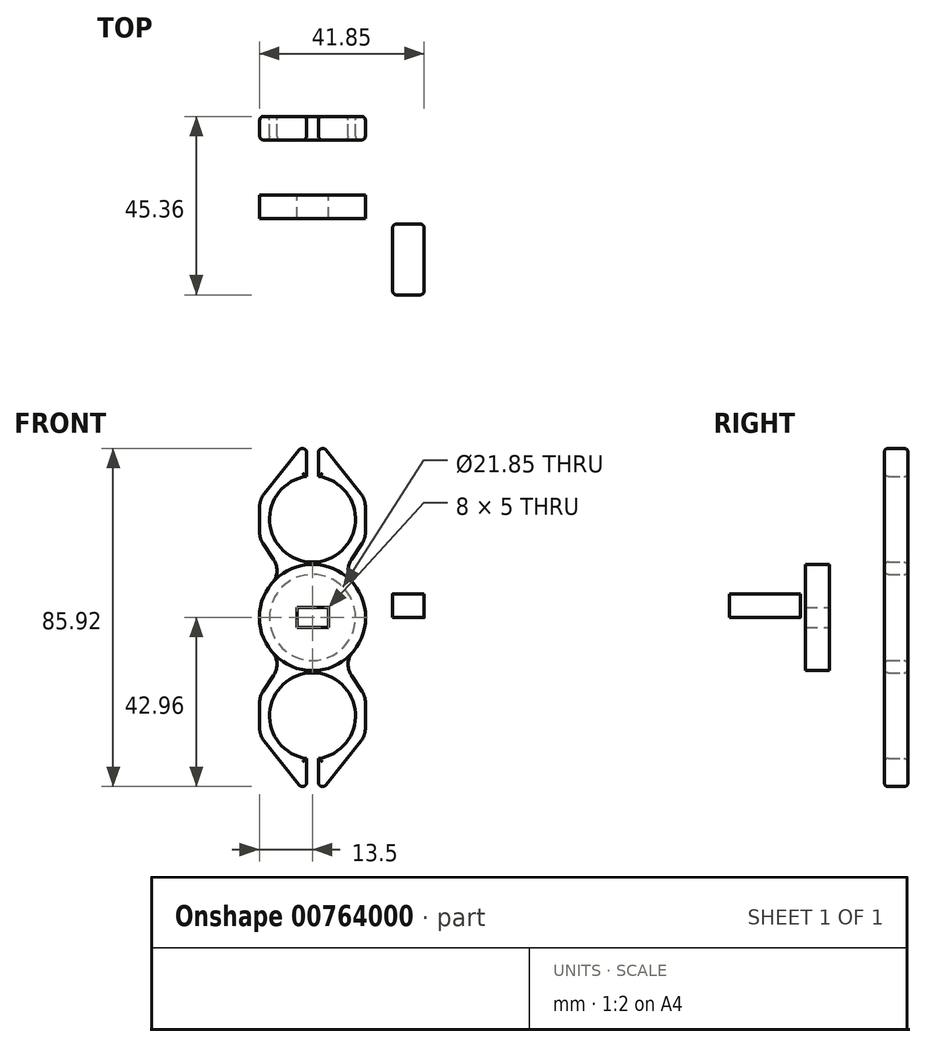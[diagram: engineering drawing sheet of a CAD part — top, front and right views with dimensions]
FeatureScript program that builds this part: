
annotation { "Feature Type Name" : "Feature", "Feature Type Description" : "" }
export const myFeature = defineFeature(function(context is Context, id is Id, definition is map)
    precondition{}
    {
        {
            var Q0;
            Q0=qCreatedBy(makeId("Front.planeOp"),FACE);
            var sketch = newSketch(context, id + "F0", { "sketchPlane" : qUnion([Q0])});
            skCircle(sketch, "E0", {"center": v(0, 0) * mm, "radius": 10.93 * mm});
            skLineSegment(sketch, "E1", {"start": v(0, 0) * mm, "end": v(0, 25) * mm, "construction": true});
            skArc(sketch, "E2", {"start": v(-1.5, 35.32) * mm, "mid": v(0, 14.58) * mm, "end": v(1.5, 35.32) * mm});
            skArc(sketch, "E3.1.0", {"start": v(1.5, -35.32) * mm, "mid": v(0, -14.58) * mm, "end": v(-1.5, -35.32) * mm});
            skLineSegment(sketch, "E4.left", {"start": v(1.5, -41.86) * mm, "end": v(1.5, -35.32) * mm});
            skLineSegment(sketch, "E4.right", {"start": v(-1.5, -41.86) * mm, "end": v(-1.5, -35.32) * mm});
            skLineSegment(sketch, "E5.left", {"start": v(13.42, -28.26) * mm, "end": v(13.42, -21.51) * mm});
            skLineSegment(sketch, "E5.right", {"start": v(-13.42, -28.26) * mm, "end": v(-13.42, -21.51) * mm});
            skLineSegment(sketch, "E6.left", {"start": v(13.42, 21.51) * mm, "end": v(13.42, 28.26) * mm});
            skLineSegment(sketch, "E6.right", {"start": v(-13.42, 21.51) * mm, "end": v(-13.42, 28.26) * mm});
            skLineSegment(sketch, "E7", {"start": v(12.33, 31.37) * mm, "end": v(3.45, 42.54) * mm});
            skLineSegment(sketch, "E8", {"start": v(-3.45, 42.54) * mm, "end": v(-12.33, 31.37) * mm});
            skArc(sketch, "E9", {"start": v(10.23, -8.68) * mm, "mid": v(13.42, 0) * mm, "end": v(10.23, 8.68) * mm});
            skLineSegment(sketch, "E10", {"start": v(12.33, -31.37) * mm, "end": v(3.45, -42.54) * mm});
            skLineSegment(sketch, "E11", {"start": v(-3.45, -42.54) * mm, "end": v(-12.33, -31.37) * mm});
            skLineSegment(sketch, "E12", {"start": v(12.58, -18.74) * mm, "end": v(9.88, -14.7) * mm});
            skLineSegment(sketch, "E13", {"start": v(-9.88, -14.7) * mm, "end": v(-12.58, -18.74) * mm});
            skLineSegment(sketch, "E14", {"start": v(12.58, 18.74) * mm, "end": v(9.88, 14.7) * mm});
            skLineSegment(sketch, "E15", {"start": v(-9.88, 14.7) * mm, "end": v(-12.58, 18.74) * mm});
            skLineSegment(sketch, "E16.trimOffspring", {"start": v(1.5, 35.32) * mm, "end": v(1.5, 41.86) * mm});
            skLineSegment(sketch, "E17.trimOffspring", {"start": v(-1.5, 35.32) * mm, "end": v(-1.5, 41.86) * mm});
            skArc(sketch, "E18.trimOffspring", {"start": v(-10.23, 8.68) * mm, "mid": v(-13.42, 0) * mm, "end": v(-10.23, -8.68) * mm});
            skPoint(sketch, "E19.visualSharp", {"position": v(13.42, 30) * mm});
            skArc(sketch, "E19.filletArc", {"start": v(13.42, 28.26) * mm, "mid": v(13.14, 29.9) * mm, "end": v(12.33, 31.37) * mm});
            skPoint(sketch, "E20.visualSharp", {"position": v(13.42, 20) * mm});
            skArc(sketch, "E20.filletArc", {"start": v(12.58, 18.74) * mm, "mid": v(13.2, 20.07) * mm, "end": v(13.42, 21.51) * mm});
            skPoint(sketch, "E21.visualSharp", {"position": v(-13.42, 20) * mm});
            skArc(sketch, "E21.filletArc", {"start": v(-13.42, 21.51) * mm, "mid": v(-13.2, 20.07) * mm, "end": v(-12.58, 18.74) * mm});
            skPoint(sketch, "E22.visualSharp", {"position": v(-13.42, 30) * mm});
            skArc(sketch, "E22.filletArc", {"start": v(-12.33, 31.37) * mm, "mid": v(-13.14, 29.9) * mm, "end": v(-13.42, 28.26) * mm});
            skPoint(sketch, "E23.visualSharp", {"position": v(-1.5, 45) * mm});
            skArc(sketch, "E23.filletArc", {"start": v(-1.5, 41.86) * mm, "mid": v(-2.23, 42.9) * mm, "end": v(-3.45, 42.54) * mm});
            skPoint(sketch, "E24.visualSharp", {"position": v(1.5, 45) * mm});
            skArc(sketch, "E24.filletArc", {"start": v(3.45, 42.54) * mm, "mid": v(2.23, 42.9) * mm, "end": v(1.5, 41.86) * mm});
            skPoint(sketch, "E25.visualSharp", {"position": v(13.42, -20) * mm});
            skArc(sketch, "E25.filletArc", {"start": v(13.42, -21.51) * mm, "mid": v(13.2, -20.07) * mm, "end": v(12.58, -18.74) * mm});
            skPoint(sketch, "E26.visualSharp", {"position": v(13.42, -30) * mm});
            skArc(sketch, "E26.filletArc", {"start": v(12.33, -31.37) * mm, "mid": v(13.14, -29.9) * mm, "end": v(13.42, -28.26) * mm});
            skPoint(sketch, "E27.visualSharp", {"position": v(1.5, -45) * mm});
            skArc(sketch, "E27.filletArc", {"start": v(1.5, -41.86) * mm, "mid": v(2.23, -42.9) * mm, "end": v(3.45, -42.54) * mm});
            skPoint(sketch, "E28.visualSharp", {"position": v(-1.5, -45) * mm});
            skArc(sketch, "E28.filletArc", {"start": v(-3.45, -42.54) * mm, "mid": v(-2.23, -42.9) * mm, "end": v(-1.5, -41.86) * mm});
            skPoint(sketch, "E29.visualSharp", {"position": v(-13.42, -30) * mm});
            skArc(sketch, "E29.filletArc", {"start": v(-13.42, -28.26) * mm, "mid": v(-13.14, -29.9) * mm, "end": v(-12.33, -31.37) * mm});
            skPoint(sketch, "E30.visualSharp", {"position": v(-13.42, -20) * mm});
            skArc(sketch, "E30.filletArc", {"start": v(-12.58, -18.74) * mm, "mid": v(-13.2, -20.07) * mm, "end": v(-13.42, -21.51) * mm});
            skPoint(sketch, "E31.visualSharp", {"position": v(7.5, -11.13) * mm});
            skArc(sketch, "E31.filletArc", {"start": v(10.23, -8.68) * mm, "mid": v(9.05, -11.63) * mm, "end": v(9.88, -14.7) * mm});
            skPoint(sketch, "E32.visualSharp", {"position": v(-7.5, -11.13) * mm});
            skArc(sketch, "E32.filletArc", {"start": v(-9.88, -14.7) * mm, "mid": v(-9.05, -11.63) * mm, "end": v(-10.23, -8.68) * mm});
            skPoint(sketch, "E33.visualSharp", {"position": v(7.5, 11.13) * mm});
            skArc(sketch, "E33.filletArc", {"start": v(9.88, 14.7) * mm, "mid": v(9.05, 11.63) * mm, "end": v(10.23, 8.68) * mm});
            skPoint(sketch, "E34.visualSharp", {"position": v(-7.5, 11.13) * mm});
            skArc(sketch, "E34.filletArc", {"start": v(-10.23, 8.68) * mm, "mid": v(-9.05, 11.63) * mm, "end": v(-9.88, 14.7) * mm});
            skCircle(sketch, "E35", {"center": v(0, 25) * mm, "radius": 10.93 * mm});
            skCircle(sketch, "E36", {"center": v(0, -25) * mm, "radius": 10.93 * mm});
            skSolve(sketch);
        }
        {
            var Q0;
            Q0=makeQuery(id+"F0.imprint","IMPRINT",FACE,{"disambiguationData":[TD([[makeQuery(id+"F0.imprint","IMPRINT",EDGE,{"derivedFrom":sQuery(id+"F0.wireOp",EDGE,"E0")}),-1.0]])]});
            extrude(context, id + "F1", {"entities" : qUnion([Q0]), "depth" : 6 * mm, "offsetDistance" : 25 * mm});
        }
        {
            var Q0;
            Q0=makeQuery(id+"F1.opExtrude","CAP_FACE",FACE,{"disambiguationData":[OSD([sQuery(id+"F0.wireOp",EDGE,"E0"),sQuery(id+"F0.wireOp",EDGE,"E2"),sQuery(id+"F0.wireOp",EDGE,"E3.1.0"),sQuery(id+"F0.wireOp",EDGE,"E3.2.0"),sQuery(id+"F0.wireOp",EDGE,"E3.3.0"),sQuery(id+"F0.wireOp",EDGE,"E3.4.0"),sQuery(id+"F0.wireOp",EDGE,"6w4LuyIg-Judz-7qcx-iNhM-kCVs0XRHMAQz.left"),sQuery(id+"F0.wireOp",EDGE,"6w4LuyIg-Judz-7qcx-iNhM-kCVs0XRHMAQz.right"),sQuery(id+"F0.wireOp",EDGE,"GuxD1Two-tXSI-jhGi-diOq-QsG6SmieNdRW"),sQuery(id+"F0.wireOp",EDGE,"9e989a9f-be13-4d0f-822f-95c7c0624428.1.0"),sQuery(id+"F0.wireOp",EDGE,"9e989a9f-be13-4d0f-822f-95c7c0624428.1.1"),sQuery(id+"F0.wireOp",EDGE,"9e989a9f-be13-4d0f-822f-95c7c0624428.1.2"),sQuery(id+"F0.wireOp",EDGE,"9e989a9f-be13-4d0f-822f-95c7c0624428.2.0"),sQuery(id+"F0.wireOp",EDGE,"9e989a9f-be13-4d0f-822f-95c7c0624428.2.1"),sQuery(id+"F0.wireOp",EDGE,"9e989a9f-be13-4d0f-822f-95c7c0624428.2.2"),sQuery(id+"F0.wireOp",EDGE,"9e989a9f-be13-4d0f-822f-95c7c0624428.3.0"),sQuery(id+"F0.wireOp",EDGE,"9e989a9f-be13-4d0f-822f-95c7c0624428.3.1"),sQuery(id+"F0.wireOp",EDGE,"9e989a9f-be13-4d0f-822f-95c7c0624428.3.2"),sQuery(id+"F0.wireOp",EDGE,"9e989a9f-be13-4d0f-822f-95c7c0624428.4.0"),sQuery(id+"F0.wireOp",EDGE,"9e989a9f-be13-4d0f-822f-95c7c0624428.4.1"),sQuery(id+"F0.wireOp",EDGE,"9e989a9f-be13-4d0f-822f-95c7c0624428.4.2"),sQuery(id+"F0.wireOp",EDGE,"486a15bc-75c9-41d0-808c-e5c4775e6e80.filletArc"),sQuery(id+"F0.wireOp",EDGE,"d314a861-2769-46d2-9bec-117903992242.filletArc"),sQuery(id+"F0.wireOp",EDGE,"5d220be9-c9be-4508-b7a3-f434c5fdea58.filletArc"),sQuery(id+"F0.wireOp",EDGE,"2974d6c2-e4a2-45df-9bc2-224e587c2884.filletArc"),sQuery(id+"F0.wireOp",EDGE,"3265ed39-f9f2-4246-9e43-8a9d8c4dec78.filletArc")])],"isStart":false});
            var Q1;
            Q1=makeQuery(id+"F1.opExtrude","CAP_FACE",FACE,{"disambiguationData":[OSD([sQuery(id+"F0.wireOp",EDGE,"E0"),sQuery(id+"F0.wireOp",EDGE,"E2"),sQuery(id+"F0.wireOp",EDGE,"E3.1.0"),sQuery(id+"F0.wireOp",EDGE,"E3.2.0"),sQuery(id+"F0.wireOp",EDGE,"E3.3.0"),sQuery(id+"F0.wireOp",EDGE,"E3.4.0"),sQuery(id+"F0.wireOp",EDGE,"6w4LuyIg-Judz-7qcx-iNhM-kCVs0XRHMAQz.left"),sQuery(id+"F0.wireOp",EDGE,"6w4LuyIg-Judz-7qcx-iNhM-kCVs0XRHMAQz.right"),sQuery(id+"F0.wireOp",EDGE,"GuxD1Two-tXSI-jhGi-diOq-QsG6SmieNdRW"),sQuery(id+"F0.wireOp",EDGE,"9e989a9f-be13-4d0f-822f-95c7c0624428.1.0"),sQuery(id+"F0.wireOp",EDGE,"9e989a9f-be13-4d0f-822f-95c7c0624428.1.1"),sQuery(id+"F0.wireOp",EDGE,"9e989a9f-be13-4d0f-822f-95c7c0624428.1.2"),sQuery(id+"F0.wireOp",EDGE,"9e989a9f-be13-4d0f-822f-95c7c0624428.2.0"),sQuery(id+"F0.wireOp",EDGE,"9e989a9f-be13-4d0f-822f-95c7c0624428.2.1"),sQuery(id+"F0.wireOp",EDGE,"9e989a9f-be13-4d0f-822f-95c7c0624428.2.2"),sQuery(id+"F0.wireOp",EDGE,"9e989a9f-be13-4d0f-822f-95c7c0624428.3.0"),sQuery(id+"F0.wireOp",EDGE,"9e989a9f-be13-4d0f-822f-95c7c0624428.3.1"),sQuery(id+"F0.wireOp",EDGE,"9e989a9f-be13-4d0f-822f-95c7c0624428.3.2"),sQuery(id+"F0.wireOp",EDGE,"9e989a9f-be13-4d0f-822f-95c7c0624428.4.0"),sQuery(id+"F0.wireOp",EDGE,"9e989a9f-be13-4d0f-822f-95c7c0624428.4.1"),sQuery(id+"F0.wireOp",EDGE,"9e989a9f-be13-4d0f-822f-95c7c0624428.4.2"),sQuery(id+"F0.wireOp",EDGE,"486a15bc-75c9-41d0-808c-e5c4775e6e80.filletArc"),sQuery(id+"F0.wireOp",EDGE,"d314a861-2769-46d2-9bec-117903992242.filletArc"),sQuery(id+"F0.wireOp",EDGE,"5d220be9-c9be-4508-b7a3-f434c5fdea58.filletArc"),sQuery(id+"F0.wireOp",EDGE,"2974d6c2-e4a2-45df-9bc2-224e587c2884.filletArc"),sQuery(id+"F0.wireOp",EDGE,"3265ed39-f9f2-4246-9e43-8a9d8c4dec78.filletArc")])],"isStart":true});
            fillet(context, id + "F2", {"entities" : qUnion([Q0, Q1]), "radius" : 1 * mm, "tangentPropagation" : true, "allowEdgeOverflow" : false});
        }
        {
            var Q0;
            Q0=qCreatedBy(makeId("Top.planeOp"),FACE);
            var sketch = newSketch(context, id + "F3", { "sketchPlane" : qUnion([Q0])});
            skLineSegment(sketch, "E37.bottom", {"start": v(21.35, -27.36) * mm, "end": v(27.35, -27.36) * mm});
            skLineSegment(sketch, "E37.top", {"start": v(21.35, -45.36) * mm, "end": v(27.35, -45.36) * mm});
            skLineSegment(sketch, "E37.left", {"start": v(20.35, -28.36) * mm, "end": v(20.35, -44.36) * mm});
            skLineSegment(sketch, "E37.right", {"start": v(28.35, -28.36) * mm, "end": v(28.35, -44.36) * mm});
            skPoint(sketch, "E37.middle", {"position": v(24.35, -36.36) * mm});
            skPoint(sketch, "E38.visualSharp", {"position": v(20.35, -45.36) * mm});
            skArc(sketch, "E38.filletArc", {"start": v(20.35, -44.36) * mm, "mid": v(20.64, -45.06) * mm, "end": v(21.35, -45.36) * mm});
            skPoint(sketch, "E39.visualSharp", {"position": v(28.35, -45.36) * mm});
            skArc(sketch, "E39.filletArc", {"start": v(27.35, -45.36) * mm, "mid": v(28.05, -45.06) * mm, "end": v(28.35, -44.36) * mm});
            skPoint(sketch, "E40.visualSharp", {"position": v(28.35, -27.36) * mm});
            skArc(sketch, "E40.filletArc", {"start": v(28.35, -28.36) * mm, "mid": v(28.05, -27.65) * mm, "end": v(27.35, -27.36) * mm});
            skPoint(sketch, "E41.visualSharp", {"position": v(20.35, -27.36) * mm});
            skArc(sketch, "E41.filletArc", {"start": v(21.35, -27.36) * mm, "mid": v(20.64, -27.65) * mm, "end": v(20.35, -28.36) * mm});
            skSolve(sketch);
        }
        {
            var Q0;
            Q0=makeQuery(id+"F3.imprint","IMPRINT",FACE,{"disambiguationData":[TD([[makeQuery(id+"F3.imprint","IMPRINT",EDGE,{"derivedFrom":sQuery(id+"F3.wireOp",EDGE,"E37.bottom")}),-1.0]])]});
            extrude(context, id + "F4", {"entities" : qUnion([Q0]), "depth" : 6 * mm, "offsetDistance" : 25 * mm});
        }
        {
            var Q0;
            Q0=qCreatedBy(makeId("Front.planeOp"),FACE);
            var sketch = newSketch(context, id + "F5", { "sketchPlane" : qUnion([Q0])});
            skCircle(sketch, "E42", {"center": v(0, 0) * mm, "radius": 13.5 * mm});
            skLineSegment(sketch, "E43.bottom", {"start": v(4, -2.5) * mm, "end": v(-4, -2.5) * mm});
            skLineSegment(sketch, "E43.top", {"start": v(4, 2.5) * mm, "end": v(-4, 2.5) * mm});
            skLineSegment(sketch, "E43.left", {"start": v(4, -2.5) * mm, "end": v(4, 2.5) * mm});
            skLineSegment(sketch, "E43.right", {"start": v(-4, -2.5) * mm, "end": v(-4, 2.5) * mm});
            skSolve(sketch);
        }
        {
            var Q0;
            Q0=qSketchRegion(id+"F5",true);
            extrude(context, id + "F6", {"entities" : qUnion([Q0]), "depth" : 26 * mm, "offsetDistance" : 25 * mm, "hasSecondDirection" : true, "secondDirectionOppositeDirection" : false, "secondDirectionDepth" : 20 * mm});
        }
    });
